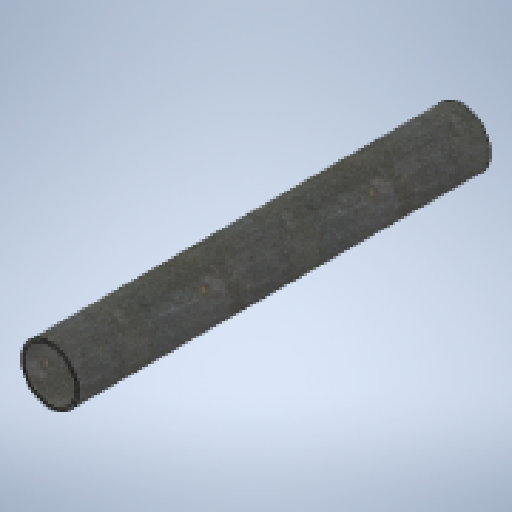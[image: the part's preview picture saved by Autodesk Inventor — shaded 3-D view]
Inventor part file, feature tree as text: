
AUTODESK INVENTOR PART (.ipt)
format: ipt  version: 2025.1 (Build 291241020, 241B)  size: 150,016 bytes
history: native  units: mm
features: extrude x1, sketch x1
ambient origin geometry x8: Origin, YZ Plane, XZ Plane, XY Plane, X Axis, Y Axis, Z Axis, Center Point
bodies: Solid1 (feature_tree)
feature tree (2):
  extrude  "Extrusion1"  Depth=430.0mm
  sketch  "Sketch1"  dims[d0=60.0mm d1=3.0mm d2=430.0mm d3=0.0mm]
